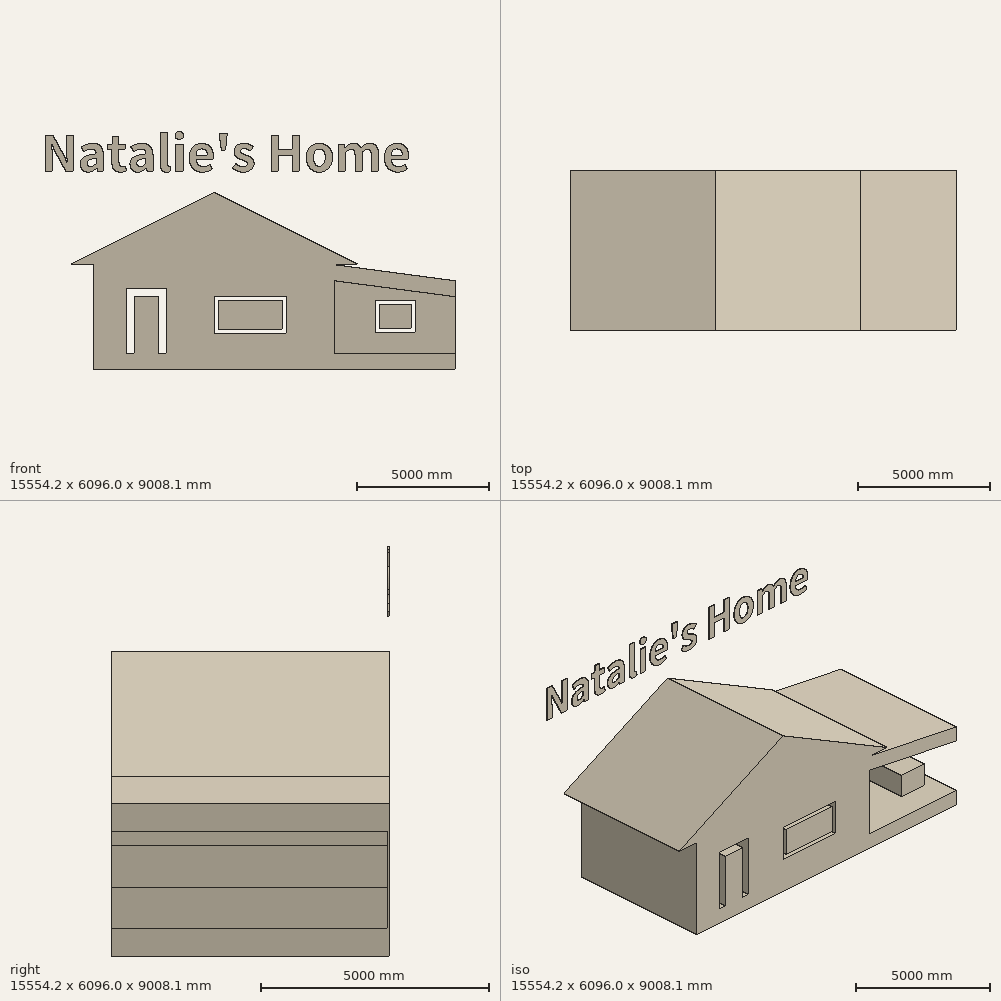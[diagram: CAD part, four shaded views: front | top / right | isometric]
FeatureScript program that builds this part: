
annotation { "Feature Type Name" : "Feature", "Feature Type Description" : "" }
export const myFeature = defineFeature(function(context is Context, id is Id, definition is map)
    precondition{}
    {
        {
            var Q0;
            Q0=qCreatedBy(makeId("Front.planeOp"),FACE);
            var sketch = newSketch(context, id + "F0", { "sketchPlane" : qUnion([Q0])});
            skLineSegment(sketch, "E0", {"start": v(0, 0) * mm, "end": v(-9144, 0) * mm});
            skLineSegment(sketch, "E1", {"start": v(-9144, 0) * mm, "end": v(-9144, 609.6) * mm});
            skLineSegment(sketch, "E2", {"start": v(0, 0) * mm, "end": v(0, 609.6) * mm});
            skLineSegment(sketch, "E3", {"start": v(0, 609.6) * mm, "end": v(-9144, 609.6) * mm});
            skLineSegment(sketch, "E4", {"start": v(0, 609.6) * mm, "end": v(0, 3962.4) * mm});
            skLineSegment(sketch, "E5", {"start": v(-9144, 609.6) * mm, "end": v(-9144, 3962.4) * mm});
            skLineSegment(sketch, "E6", {"start": v(-9144, 3962.4) * mm, "end": v(-10058.4, 3962.4) * mm});
            skLineSegment(sketch, "E7", {"start": v(0, 3962.4) * mm, "end": v(914.4, 3962.4) * mm});
            skLineSegment(sketch, "E8", {"start": v(-9144, 3962.4) * mm, "end": v(-4572, 3962.4) * mm});
            skLineSegment(sketch, "E9", {"start": v(-4572, 3962.4) * mm, "end": v(-4572, 6248.4) * mm});
            skLineSegment(sketch, "E10", {"start": v(0, 3962.4) * mm, "end": v(-4572, 3962.4) * mm});
            skLineSegment(sketch, "E11", {"start": v(-4572, 6248.4) * mm, "end": v(-4572, 6705.6) * mm});
            skLineSegment(sketch, "E12", {"start": v(-4572, 6705.6) * mm, "end": v(914.4, 3962.4) * mm});
            skLineSegment(sketch, "E13", {"start": v(-4572, 6248.4) * mm, "end": v(0, 3962.4) * mm});
            skLineSegment(sketch, "E14", {"start": v(-4572, 6248.4) * mm, "end": v(-9144, 3962.4) * mm});
            skLineSegment(sketch, "E15", {"start": v(-4572, 6705.6) * mm, "end": v(-10058.4, 3962.4) * mm});
            skLineSegment(sketch, "E16", {"start": v(0, 609.6) * mm, "end": v(4572, 609.6) * mm});
            skLineSegment(sketch, "E17", {"start": v(0, 0) * mm, "end": v(4572, 0) * mm});
            skLineSegment(sketch, "E18", {"start": v(4572, 609.6) * mm, "end": v(4572, 0) * mm});
            skLineSegment(sketch, "E19", {"start": v(4572, 609.6) * mm, "end": v(4572, 3352.8) * mm});
            skLineSegment(sketch, "E20", {"start": v(0, 3962.4) * mm, "end": v(4572, 3352.8) * mm});
            skLineSegment(sketch, "E21", {"start": v(0, 3962.4) * mm, "end": v(0, 3352.8) * mm});
            skLineSegment(sketch, "E22", {"start": v(0, 3352.8) * mm, "end": v(4572, 2749.57) * mm});
            skLineSegment(sketch, "E23", {"start": v(-9144, 609.6) * mm, "end": v(-7924.8, 609.6) * mm});
            skLineSegment(sketch, "E24", {"start": v(-7924.8, 609.6) * mm, "end": v(-7620, 609.6) * mm});
            skLineSegment(sketch, "E25", {"start": v(-7620, 609.6) * mm, "end": v(-7620, 2743.2) * mm});
            skLineSegment(sketch, "E26", {"start": v(-7620, 2743.2) * mm, "end": v(-6705.6, 2743.2) * mm});
            skLineSegment(sketch, "E27", {"start": v(-6705.6, 2743.2) * mm, "end": v(-6705.6, 609.6) * mm});
            skLineSegment(sketch, "E28", {"start": v(-6705.6, 609.6) * mm, "end": v(-6400.8, 609.6) * mm});
            skLineSegment(sketch, "E29", {"start": v(-6400.8, 609.6) * mm, "end": v(-6400.8, 3048) * mm});
            skLineSegment(sketch, "E30", {"start": v(-7924.8, 609.6) * mm, "end": v(-7924.8, 3048) * mm});
            skLineSegment(sketch, "E31", {"start": v(-7924.8, 3048) * mm, "end": v(-6400.8, 3048) * mm});
            skText(sketch, "E32", { "text": "Natalie\'s Home ", "fontName": "NotoSansCJKsc-Bold.otf"});
            skPoint(sketch, "E33.startSnap0", {"position": v(-7162.8, 2743.2) * mm});
            skLineSegment(sketch, "E34", {"start": v(-4572, 2743.2) * mm, "end": v(-4572, 1371.6) * mm});
            skLineSegment(sketch, "E35", {"start": v(-4572, 2743.2) * mm, "end": v(-1828.8, 2743.2) * mm});
            skLineSegment(sketch, "E36", {"start": v(-1828.8, 2743.2) * mm, "end": v(-1828.8, 1371.6) * mm});
            skLineSegment(sketch, "E37", {"start": v(-4572, 1371.6) * mm, "end": v(-1828.8, 1371.6) * mm});
            skLineSegment(sketch, "E38.0", {"start": v(-4419.6, 2590.8) * mm, "end": v(-4419.6, 1524) * mm});
            skLineSegment(sketch, "E38.1", {"start": v(-4419.6, 2590.8) * mm, "end": v(-1981.2, 2590.8) * mm});
            skLineSegment(sketch, "E38.2", {"start": v(-1981.2, 2590.8) * mm, "end": v(-1981.2, 1524) * mm});
            skLineSegment(sketch, "E38.3", {"start": v(-4419.6, 1524) * mm, "end": v(-1981.2, 1524) * mm});
            skLineSegment(sketch, "E39.bottom", {"start": v(1676.4, 2441.41) * mm, "end": v(2895.6, 2441.41) * mm});
            skLineSegment(sketch, "E39.top", {"start": v(1676.4, 1527.01) * mm, "end": v(2895.6, 1527.01) * mm});
            skLineSegment(sketch, "E39.left", {"start": v(1676.4, 2441.41) * mm, "end": v(1676.4, 1527.01) * mm});
            skLineSegment(sketch, "E39.right", {"start": v(2895.6, 2441.41) * mm, "end": v(2895.6, 1527.01) * mm});
            skLineSegment(sketch, "E40.0", {"start": v(1524, 2593.81) * mm, "end": v(3048, 2593.81) * mm});
            skLineSegment(sketch, "E40.1", {"start": v(1524, 2593.81) * mm, "end": v(1524, 1374.61) * mm});
            skLineSegment(sketch, "E40.2", {"start": v(1524, 1374.61) * mm, "end": v(3048, 1374.61) * mm});
            skLineSegment(sketch, "E40.3", {"start": v(3048, 2593.81) * mm, "end": v(3048, 1374.61) * mm});
            const initialGuessF0  = {"E32": [-11.15168, 7.49868, 1, 0, 1.34175]};
            skSetInitialGuess(sketch, initialGuessF0);
            skSolve(sketch);
        }
        {
            var Q0;
            Q0=makeQuery(id+"F0.imprint","IMPRINT",FACE,{"disambiguationData":[TD([[makeQuery(id+"F0.imprint","IMPRINT",EDGE,{"derivedFrom":sQuery(id+"F0.wireOp",EDGE,"E8")}),1.0]])]});
            var Q1;
            Q1=makeQuery(id+"F0.imprint","IMPRINT",FACE,{"disambiguationData":[TD([[makeQuery(id+"F0.imprint","IMPRINT",EDGE,{"derivedFrom":sQuery(id+"F0.wireOp",EDGE,"E9")}),-1.0]])]});
            var Q2;
            Q2=makeQuery(id+"F0.imprint","IMPRINT",FACE,{"disambiguationData":[TD([[makeQuery(id+"F0.imprint","IMPRINT",EDGE,{"derivedFrom":sQuery(id+"F0.wireOp",EDGE,"E6")}),-1.0]])]});
            var Q3;
            Q3=makeQuery(id+"F0.imprint","IMPRINT",FACE,{"disambiguationData":[TD([[makeQuery(id+"F0.imprint","IMPRINT",EDGE,{"derivedFrom":sQuery(id+"F0.wireOp",EDGE,"E7")}),1.0]])]});
            var Q4;
            {var subQ0=sQuery(id+"F0.wireOp",EDGE,"E4");Q4=makeQuery(id+"F0.imprint","IMPRINT",FACE,{"disambiguationData":[TD([[makeQuery(id+"F0.imprint","IMPRINT",EDGE,{"derivedFrom":subQ0}),1.0]])]});}
            var Q5;
            Q5=makeQuery(id+"F0.imprint","IMPRINT",FACE,{"disambiguationData":[TD([[makeQuery(id+"F0.imprint","IMPRINT",EDGE,{"derivedFrom":sQuery(id+"F0.wireOp",EDGE,"E38.0")}),1.0]])]});
            var Q6;
            {var subQ0=sQuery(id+"F0.wireOp",EDGE,"E25");Q6=makeQuery(id+"F0.imprint","IMPRINT",FACE,{"disambiguationData":[TD([[makeQuery(id+"F0.imprint","IMPRINT",EDGE,{"derivedFrom":subQ0}),-1.0]])]});}
            var Q7;
            Q7=makeQuery(id+"F0.imprint","IMPRINT",FACE,{"disambiguationData":[TD([[makeQuery(id+"F0.imprint","IMPRINT",EDGE,{"derivedFrom":sQuery(id+"F0.wireOp",EDGE,"E0")}),-1.0]])]});
            var Q8;
            Q8=makeQuery(id+"F0.imprint","IMPRINT",FACE,{"disambiguationData":[TD([[makeQuery(id+"F0.imprint","IMPRINT",EDGE,{"derivedFrom":sQuery(id+"F0.wireOp",EDGE,"E2")}),-1.0]])]});
            var Q9;
            Q9=makeQuery(id+"F0.imprint","IMPRINT",FACE,{"disambiguationData":[TD([[makeQuery(id+"F0.imprint","IMPRINT",EDGE,{"derivedFrom":sQuery(id+"F0.wireOp",EDGE,"E4")}),-1.0]])]});
            var Q10;
            Q10=makeQuery(id+"F0.imprint","IMPRINT",FACE,{"disambiguationData":[TD([[makeQuery(id+"F0.imprint","IMPRINT",EDGE,{"derivedFrom":sQuery(id+"F0.wireOp",EDGE,"E39.bottom")}),-1.0]])]});
            var Q11;
            {var subQ0=sQuery(id+"F0.wireOp",EDGE,"E20");Q11=makeQuery(id+"F0.imprint","IMPRINT",FACE,{"disambiguationData":[TD([[makeQuery(id+"F0.imprint","IMPRINT",EDGE,{"derivedFrom":subQ0}),-1.0]])]});}
            extrude(context, id + "F1", {"entities" : qUnion([Q0, Q1, Q2, Q3, Q4, Q5, Q6, Q7, Q8, Q9, Q10, Q11]), "depth" : 6096 * mm, "offsetDistance" : 30.48 * mm});
        }
        {
            var Q0;
            Q0 = qSketchRegion(id + "F0", true);
            extrude(context, id + "F2", {"entities" : qUnion([Q0]), "operationType" : NewBodyOperationType.ADD, "depth" : 30.48 * mm, "offsetDistance" : 30.48 * mm});
        }
    });
